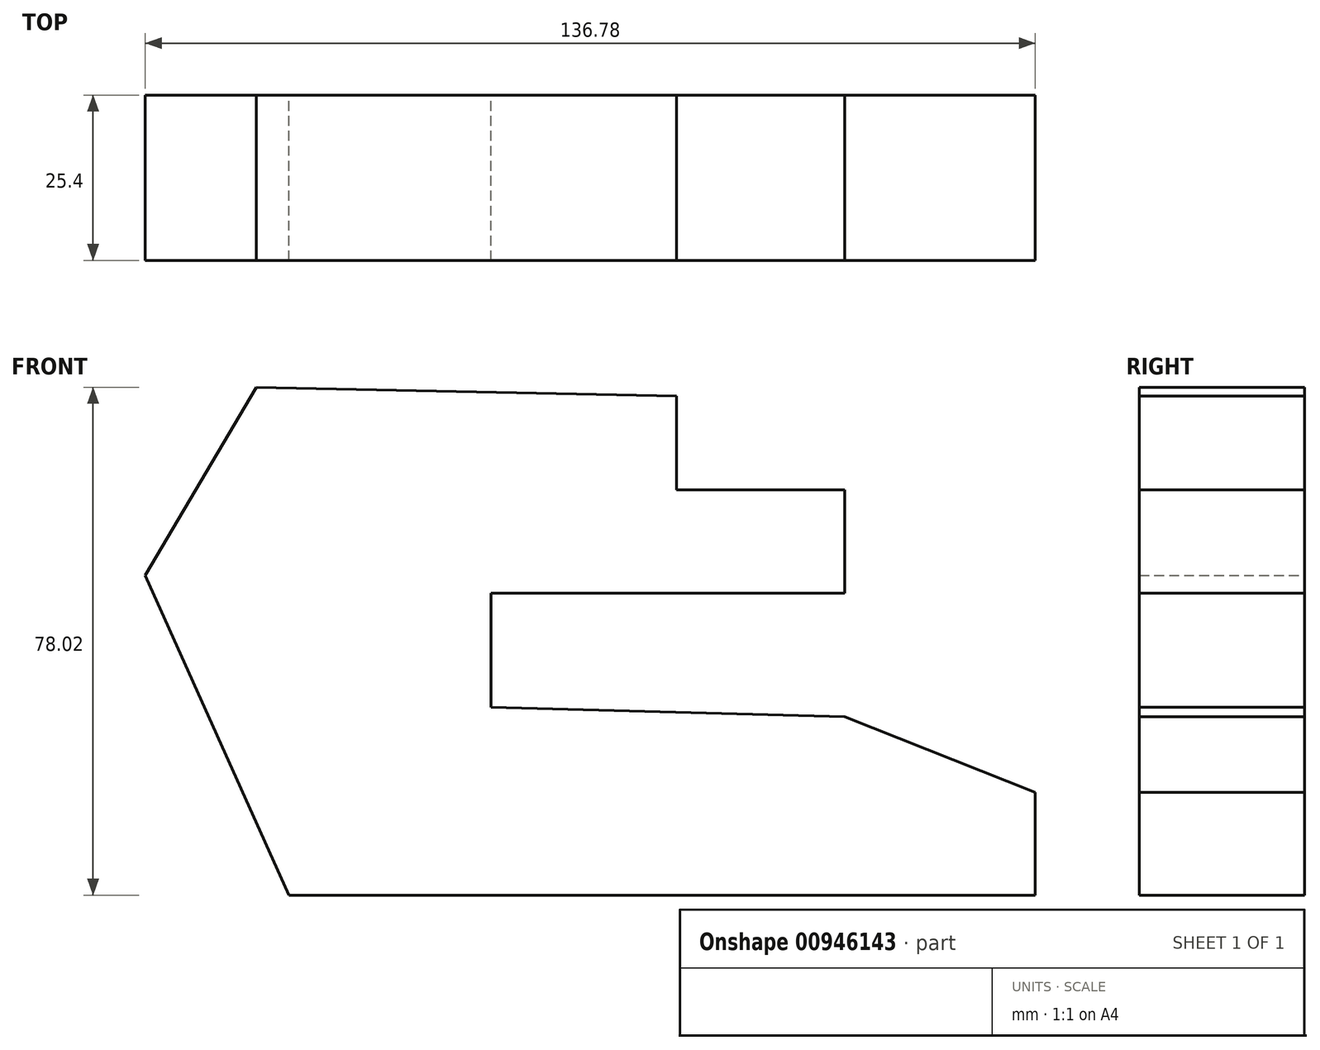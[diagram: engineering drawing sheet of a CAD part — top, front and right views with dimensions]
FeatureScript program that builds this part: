
annotation { "Feature Type Name" : "Feature", "Feature Type Description" : "" }
export const myFeature = defineFeature(function(context is Context, id is Id, definition is map)
    precondition{}
    {
        {
            var Q0;
            Q0=qCreatedBy(makeId("Front.planeOp"),FACE);
            var sketch = newSketch(context, id + "F0", { "sketchPlane" : qUnion([Q0])});
            skLineSegment(sketch, "E0", {"start": v(0, 0) * mm, "end": v(-54.36, 0) * mm});
            skLineSegment(sketch, "E1", {"start": v(-54.36, 0) * mm, "end": v(-54.36, -17.51) * mm});
            skLineSegment(sketch, "E2", {"start": v(-54.36, -17.51) * mm, "end": v(0, -19) * mm});
            skLineSegment(sketch, "E3", {"start": v(0, -19) * mm, "end": v(29.3, -30.63) * mm});
            skLineSegment(sketch, "E4", {"start": v(29.3, -30.63) * mm, "end": v(29.3, -46.4) * mm});
            skLineSegment(sketch, "E5", {"start": v(29.3, -46.4) * mm, "end": v(-85.4, -46.4) * mm});
            skLineSegment(sketch, "E6", {"start": v(-85.4, -46.4) * mm, "end": v(-107.48, 2.74) * mm});
            skLineSegment(sketch, "E7", {"start": v(-107.48, 2.74) * mm, "end": v(-90.38, 31.62) * mm});
            skLineSegment(sketch, "E8", {"start": v(-90.38, 31.62) * mm, "end": v(-25.81, 30.3) * mm});
            skLineSegment(sketch, "E9", {"start": v(-25.81, 30.3) * mm, "end": v(-25.81, 15.85) * mm});
            skLineSegment(sketch, "E10", {"start": v(-25.81, 15.85) * mm, "end": v(0, 15.85) * mm});
            skLineSegment(sketch, "E11", {"start": v(0, 15.85) * mm, "end": v(0, 0) * mm});
            skSolve(sketch);
        }
        {
            var Q0;
            Q0 = qSketchRegion(id + "F0", true);
            extrude(context, id + "F1", {"entities" : qUnion([Q0]), "depth" : 25.4 * mm, "offsetDistance" : 25.4 * mm});
        }
    });
